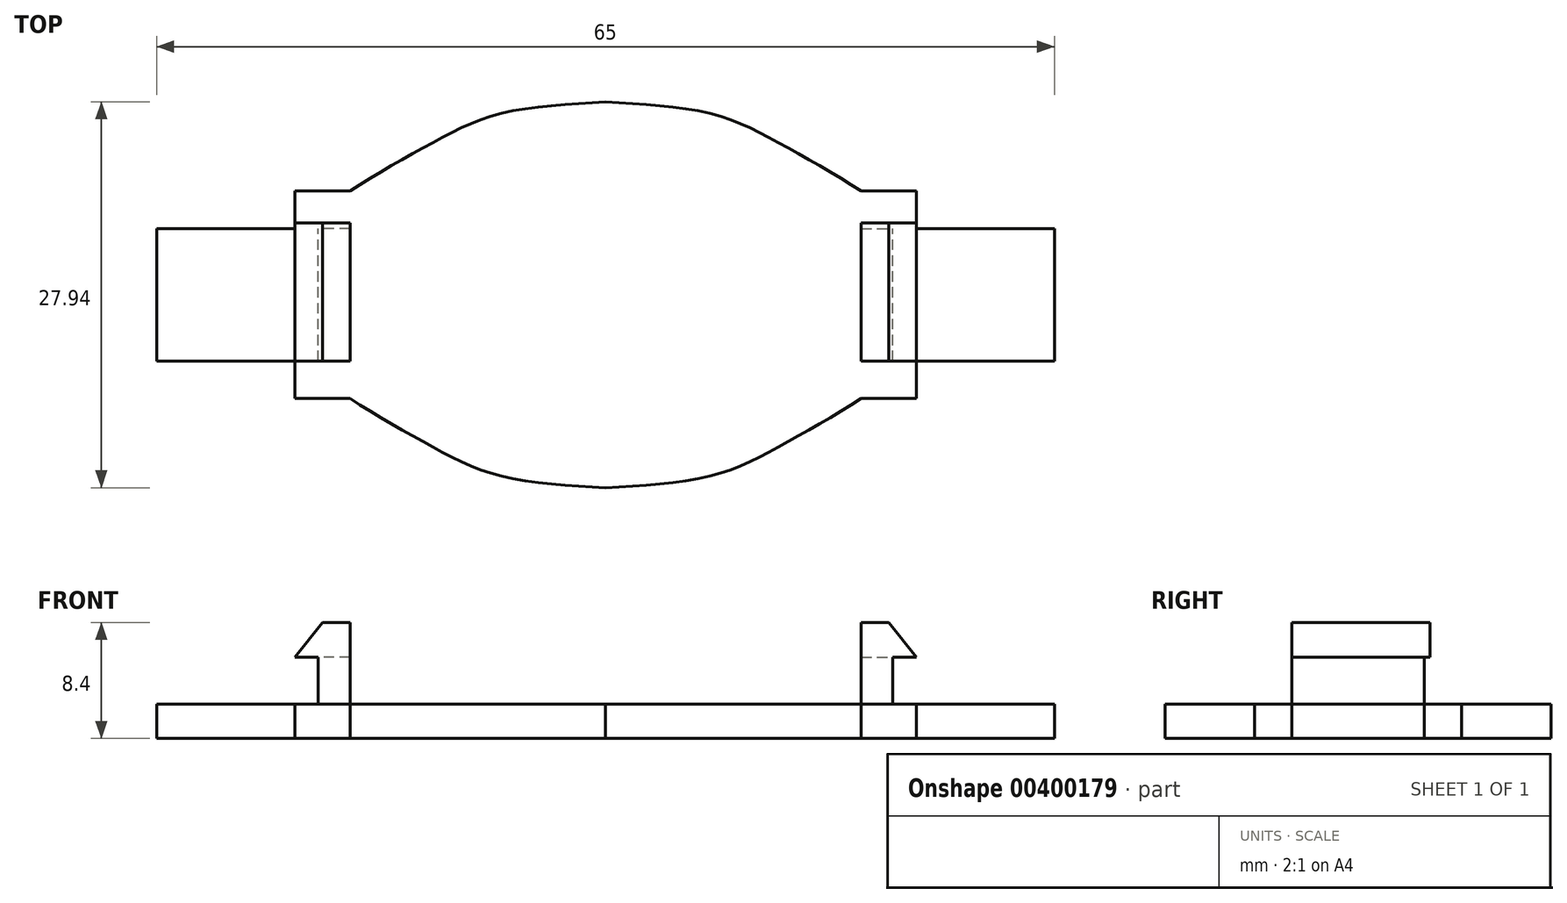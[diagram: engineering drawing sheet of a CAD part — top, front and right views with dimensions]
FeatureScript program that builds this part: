
annotation { "Feature Type Name" : "Feature", "Feature Type Description" : "" }
export const myFeature = defineFeature(function(context is Context, id is Id, definition is map)
    precondition{}
    {
        {
            var Q0;
            Q0=qCreatedBy(makeId("Top.planeOp"),FACE);
            var sketch = newSketch(context, id + "F0", { "sketchPlane" : qUnion([Q0])});
            skLineSegment(sketch, "E0", {"start": v(0, 0) * mm, "end": v(0, 40.16) * mm, "construction": true});
            skLineSegment(sketch, "E1", {"start": v(0, 0) * mm, "end": v(59.31, 0) * mm, "construction": true});
            skLineSegment(sketch, "E2", {"start": v(32.5, 0) * mm, "end": v(32.5, 4.8) * mm});
            skLineSegment(sketch, "E3", {"start": v(32.5, 4.8) * mm, "end": v(22.5, 4.8) * mm});
            skLineSegment(sketch, "E4", {"start": v(22.5, 4.8) * mm, "end": v(22.5, 7.5) * mm});
            skLineSegment(sketch, "E5", {"start": v(22.5, 7.5) * mm, "end": v(18.5, 7.5) * mm});
            skLineSegment(sketch, "E6", {"start": v(18.5, 7.6) * mm, "end": v(18.5, 7.5) * mm});
            skLineSegment(sketch, "E7.MirrorCS", {"start": v(-18.5, 5.98) * mm, "end": v(-18.5, 0) * mm});
            skLineSegment(sketch, "E8.MirrorCS", {"start": v(-22.5, 7.5) * mm, "end": v(-18.5, 7.5) * mm});
            skLineSegment(sketch, "E9.MirrorCS", {"start": v(-22.5, 4.8) * mm, "end": v(-22.5, 7.5) * mm});
            skLineSegment(sketch, "E10.MirrorCS", {"start": v(-32.5, 4.8) * mm, "end": v(-22.5, 4.8) * mm});
            skLineSegment(sketch, "E11.MirrorCS", {"start": v(-32.5, 0) * mm, "end": v(-32.5, 4.8) * mm});
            skLineSegment(sketch, "E12.MirrorCS", {"start": v(0, 0) * mm, "end": v(0, -40.16) * mm, "construction": true});
            skLineSegment(sketch, "E13.MirrorCS", {"start": v(-32.5, -4.8) * mm, "end": v(-22.5, -4.8) * mm});
            skLineSegment(sketch, "E14.MirrorCS", {"start": v(-22.5, -4.8) * mm, "end": v(-22.5, -7.5) * mm});
            skLineSegment(sketch, "E15.MirrorCS", {"start": v(32.5, -4.8) * mm, "end": v(22.5, -4.8) * mm});
            skLineSegment(sketch, "E16.MirrorCS", {"start": v(18.5, -7.6) * mm, "end": v(18.5, -7.5) * mm});
            skLineSegment(sketch, "E17.MirrorCS", {"start": v(-32.5, 0) * mm, "end": v(-32.5, -4.8) * mm});
            skLineSegment(sketch, "E18.MirrorCS", {"start": v(-18.5, -7.6) * mm, "end": v(-18.5, -7.5) * mm});
            skLineSegment(sketch, "E19.MirrorCS", {"start": v(32.5, 0) * mm, "end": v(32.5, -4.8) * mm});
            skLineSegment(sketch, "E20.MirrorCS", {"start": v(22.5, -4.8) * mm, "end": v(22.5, -7.5) * mm});
            skLineSegment(sketch, "E21.MirrorCS", {"start": v(22.5, -7.5) * mm, "end": v(18.5, -7.5) * mm});
            skLineSegment(sketch, "E22.MirrorCS", {"start": v(-22.5, -7.5) * mm, "end": v(-18.5, -7.5) * mm});
            skFitSpline(sketch, "E23", {"points": [v(-18.5, 7.5) * mm, v(-12.56, 10.98) * mm, v(-7.62, 13.1) * mm, v(0.5, 14) * mm], "startDerivative": vector(16.65, 11.13) * mm, "endDerivative": vector(22.36, 1.38) * mm});
            skFitSpline(sketch, "E24.0", {"points": [v(-17.8, 6.46) * mm, v(-17.14, 6.9) * mm, v(-15.7, 7.8) * mm, v(-13.8, 8.87) * mm, v(-12.54, 9.57) * mm, v(-11.84, 9.96) * mm, v(-11.16, 10.32) * mm, v(-10.36, 10.74) * mm, v(-9.44, 11.18) * mm, v(-8.5, 11.56) * mm, v(-7.66, 11.82) * mm, v(-6.92, 12) * mm, v(-6.13, 12.15) * mm, v(-5.07, 12.31) * mm, v(-3.7, 12.46) * mm, v(-1.8, 12.61) * mm, v(-0.36, 12.7) * mm, v(0.58, 12.75) * mm]});
            skLineSegment(sketch, "E25", {"start": v(-17.46, 6.7) * mm, "end": v(-18.5, 5.98) * mm});
            skFitSpline(sketch, "E26.MirrorCS", {"points": [v(-18.5, -7.5) * mm, v(-12.56, -10.98) * mm, v(-7.62, -13.1) * mm, v(0.5, -14) * mm], "startDerivative": vector(16.65, -11.13) * mm, "endDerivative": vector(22.36, -1.38) * mm});
            skLineSegment(sketch, "E27.MirrorCS", {"start": v(-17.46, -6.7) * mm, "end": v(-18.5, -5.98) * mm});
            skFitSpline(sketch, "E28.0", {"points": [v(-17.8, -6.46) * mm, v(-17.14, -6.9) * mm, v(-15.7, -7.8) * mm, v(-13.8, -8.87) * mm, v(-12.54, -9.57) * mm, v(-11.84, -9.96) * mm, v(-11.16, -10.32) * mm, v(-10.36, -10.74) * mm, v(-9.44, -11.18) * mm, v(-8.5, -11.56) * mm, v(-7.66, -11.82) * mm, v(-6.92, -12) * mm, v(-6.13, -12.15) * mm, v(-5.07, -12.31) * mm, v(-3.7, -12.46) * mm, v(-1.8, -12.61) * mm, v(-0.36, -12.7) * mm, v(0.58, -12.75) * mm]});
            skFitSpline(sketch, "E29.MirrorCS", {"points": [v(18.5, 7.5) * mm, v(12.56, 10.98) * mm, v(7.62, 13.1) * mm, v(-0.5, 14) * mm], "startDerivative": vector(-16.65, 11.13) * mm, "endDerivative": vector(-22.36, 1.38) * mm});
            skFitSpline(sketch, "E30.MirrorCS", {"points": [v(18.5, -7.5) * mm, v(12.56, -10.98) * mm, v(7.62, -13.1) * mm, v(-0.5, -14) * mm], "startDerivative": vector(-16.65, -11.13) * mm, "endDerivative": vector(-22.36, -1.38) * mm});
            skLineSegment(sketch, "E31.MirrorCS", {"start": v(17.46, -6.7) * mm, "end": v(18.5, -5.98) * mm});
            skLineSegment(sketch, "E32.MirrorCS", {"start": v(17.46, 6.7) * mm, "end": v(18.5, 5.98) * mm});
            skFitSpline(sketch, "E33.0", {"points": [v(17.8, 6.46) * mm, v(17.14, 6.9) * mm, v(15.7, 7.8) * mm, v(13.8, 8.87) * mm, v(12.54, 9.57) * mm, v(11.84, 9.96) * mm, v(11.16, 10.32) * mm, v(10.36, 10.74) * mm, v(9.44, 11.18) * mm, v(8.5, 11.56) * mm, v(7.66, 11.82) * mm, v(6.92, 12) * mm, v(6.13, 12.15) * mm, v(5.07, 12.31) * mm, v(3.7, 12.46) * mm, v(1.8, 12.61) * mm, v(0.36, 12.7) * mm, v(-0.58, 12.75) * mm]});
            skFitSpline(sketch, "E34.0", {"points": [v(17.8, -6.46) * mm, v(17.14, -6.9) * mm, v(15.7, -7.8) * mm, v(13.8, -8.87) * mm, v(12.54, -9.57) * mm, v(11.84, -9.96) * mm, v(11.16, -10.32) * mm, v(10.36, -10.74) * mm, v(9.44, -11.18) * mm, v(8.5, -11.56) * mm, v(7.66, -11.82) * mm, v(6.92, -12) * mm, v(6.13, -12.15) * mm, v(5.07, -12.31) * mm, v(3.7, -12.46) * mm, v(1.8, -12.61) * mm, v(0.36, -12.7) * mm, v(-0.58, -12.75) * mm]});
            skLineSegment(sketch, "E35.trimOffspring", {"start": v(-18.5, -5.98) * mm, "end": v(-18.5, 0) * mm});
            skLineSegment(sketch, "E36.trimOffspring", {"start": v(18.5, 5.98) * mm, "end": v(18.5, 0) * mm});
            skLineSegment(sketch, "E37.trimOffspring", {"start": v(18.5, -5.98) * mm, "end": v(18.5, 0) * mm});
            skLineSegment(sketch, "E38.top", {"start": v(18.5, -7.5) * mm, "end": v(18.5, -7.5) * mm});
            skLineSegment(sketch, "E38.left", {"start": v(18.5, 5) * mm, "end": v(18.5, -5.98) * mm});
            skSolve(sketch);
        }
        {
            var Q0;
            Q0=makeQuery(id+"F0.imprint","IMPRINT",FACE,{"disambiguationData":[TD([[makeQuery(id+"F0.imprint","IMPRINT",EDGE,{"derivedFrom":sQuery(id+"F0.wireOp",EDGE,"E2")}),1.0]])]});
            extrude(context, id + "F1", {"entities" : qUnion([Q0]), "oppositeDirection" : true, "depth" : 2.5 * mm});
        }
        {
            var Q0;
            Q0=makeQuery(id+"F1.opExtrude","CAP_FACE",FACE,{"disambiguationData":[OSD([sQuery(id+"F0.wireOp",EDGE,"E2"),sQuery(id+"F0.wireOp",EDGE,"E3"),sQuery(id+"F0.wireOp",EDGE,"E4"),sQuery(id+"F0.wireOp",EDGE,"E5"),sQuery(id+"F0.wireOp",EDGE,"E7.MirrorCS"),sQuery(id+"F0.wireOp",EDGE,"E8.MirrorCS"),sQuery(id+"F0.wireOp",EDGE,"E9.MirrorCS"),sQuery(id+"F0.wireOp",EDGE,"E10.MirrorCS"),sQuery(id+"F0.wireOp",EDGE,"E11.MirrorCS"),sQuery(id+"F0.wireOp",EDGE,"E13.MirrorCS"),sQuery(id+"F0.wireOp",EDGE,"E14.MirrorCS"),sQuery(id+"F0.wireOp",EDGE,"E15.MirrorCS"),sQuery(id+"F0.wireOp",EDGE,"E17.MirrorCS"),sQuery(id+"F0.wireOp",EDGE,"E19.MirrorCS"),sQuery(id+"F0.wireOp",EDGE,"E20.MirrorCS"),sQuery(id+"F0.wireOp",EDGE,"E21.MirrorCS"),sQuery(id+"F0.wireOp",EDGE,"E22.MirrorCS"),sQuery(id+"F0.wireOp",EDGE,"E23"),sQuery(id+"F0.wireOp",EDGE,"E24.0"),sQuery(id+"F0.wireOp",EDGE,"E25"),sQuery(id+"F0.wireOp",EDGE,"E26.MirrorCS"),sQuery(id+"F0.wireOp",EDGE,"E27.MirrorCS"),sQuery(id+"F0.wireOp",EDGE,"E28.0"),sQuery(id+"F0.wireOp",EDGE,"E29.MirrorCS"),sQuery(id+"F0.wireOp",EDGE,"E30.MirrorCS"),sQuery(id+"F0.wireOp",EDGE,"E31.MirrorCS"),sQuery(id+"F0.wireOp",EDGE,"E32.MirrorCS"),sQuery(id+"F0.wireOp",EDGE,"E33.0"),sQuery(id+"F0.wireOp",EDGE,"E34.0"),sQuery(id+"F0.wireOp",EDGE,"E35.trimOffspring"),sQuery(id+"F0.wireOp",EDGE,"E36.trimOffspring"),sQuery(id+"F0.wireOp",EDGE,"E38.top"),sQuery(id+"F0.wireOp",EDGE,"E38.left")])],"isStart":true});
            var sketch = newSketch(context, id + "F2", { "sketchPlane" : qUnion([Q0])});
            skLineSegment(sketch, "E39", {"start": v(22.5, -4.8) * mm, "end": v(18.5, -4.8) * mm, "construction": true});
            skLineSegment(sketch, "E40.bottom", {"start": v(18.5, -4.8) * mm, "end": v(20.8, -4.8) * mm});
            skLineSegment(sketch, "E40.top", {"start": v(18.5, 4.8) * mm, "end": v(20.8, 4.8) * mm});
            skLineSegment(sketch, "E40.left", {"start": v(18.5, -4.8) * mm, "end": v(18.5, 4.8) * mm});
            skLineSegment(sketch, "E40.right", {"start": v(20.8, -4.8) * mm, "end": v(20.8, 4.8) * mm});
            skLineSegment(sketch, "E41.MirrorCS", {"start": v(-18.5, -4.8) * mm, "end": v(-18.5, 4.8) * mm});
            skLineSegment(sketch, "E42.MirrorCS", {"start": v(-18.5, 4.8) * mm, "end": v(-20.8, 4.8) * mm});
            skLineSegment(sketch, "E43.MirrorCS", {"start": v(-20.8, -4.8) * mm, "end": v(-20.8, 4.8) * mm});
            skLineSegment(sketch, "E44.MirrorCS", {"start": v(-22.5, -4.8) * mm, "end": v(-18.5, -4.8) * mm, "construction": true});
            skLineSegment(sketch, "E45.MirrorCS", {"start": v(-18.5, -4.8) * mm, "end": v(-20.8, -4.8) * mm});
            skSolve(sketch);
        }
        {
            var Q0;
            Q0 = qSketchRegion(id + "F2", true);
            extrude(context, id + "F3", {"entities" : qUnion([Q0]), "operationType" : NewBodyOperationType.ADD, "depth" : 3.4 * mm});
        }
        {
            var Q0;
            Q0=makeQuery(id+"F3.opExtrude","SWEPT_FACE",FACE,{"disambiguationData":[OSD([sQuery(id+"F2.wireOp",EDGE,"E40.bottom")])]});
            var sketch = newSketch(context, id + "F4", { "sketchPlane" : qUnion([Q0])});
            skLineSegment(sketch, "E46.bottom", {"start": v(18.5, 3.4) * mm, "end": v(22.5, 3.4) * mm});
            skLineSegment(sketch, "E46.top", {"start": v(18.5, 5.9) * mm, "end": v(20.5, 5.9) * mm});
            skLineSegment(sketch, "E46.left", {"start": v(18.5, 3.4) * mm, "end": v(18.5, 5.9) * mm});
            skLineSegment(sketch, "E47", {"start": v(22.5, 3.4) * mm, "end": v(20.5, 5.9) * mm});
            skPoint(sketch, "E46.right.end.orphan", {"position": v(22.5, 5.9) * mm});
            skLineSegment(sketch, "E48.MirrorCS", {"start": v(-22.5, 3.4) * mm, "end": v(-20.5, 5.9) * mm});
            skLineSegment(sketch, "E49.MirrorCS", {"start": v(-18.5, 3.4) * mm, "end": v(-22.5, 3.4) * mm});
            skLineSegment(sketch, "E50.MirrorCS", {"start": v(-18.5, 3.4) * mm, "end": v(-18.5, 5.9) * mm});
            skLineSegment(sketch, "E51.MirrorCS", {"start": v(-18.5, 5.9) * mm, "end": v(-20.5, 5.9) * mm});
            skSolve(sketch);
        }
        {
            var Q0;
            Q0 = qSketchRegion(id + "F4", true);
            extrude(context, id + "F5", {"entities" : qUnion([Q0]), "operationType" : NewBodyOperationType.ADD, "oppositeDirection" : true, "depth" : 10 * mm});
        }
    });
